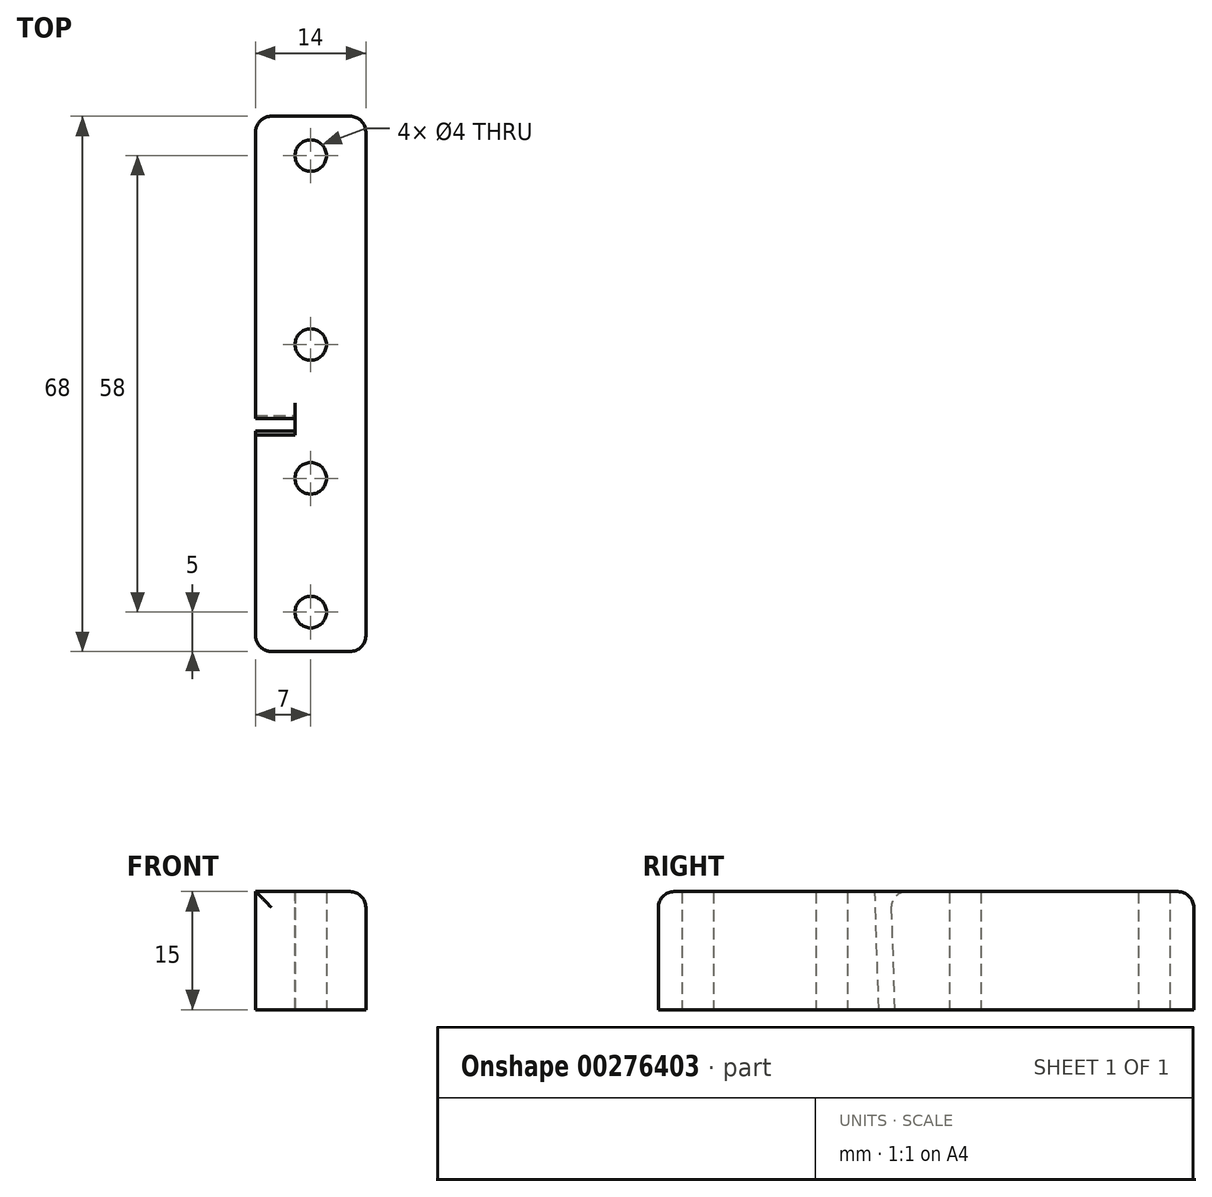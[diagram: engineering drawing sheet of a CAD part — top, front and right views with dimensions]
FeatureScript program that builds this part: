
annotation { "Feature Type Name" : "Feature", "Feature Type Description" : "" }
export const myFeature = defineFeature(function(context is Context, id is Id, definition is map)
    precondition{}
    {
        {
            var Q0;
            Q0=qCreatedBy(makeId("Top.planeOp"),FACE);
            var sketch = newSketch(context, id + "F0", { "sketchPlane" : qUnion([Q0])});
            skLineSegment(sketch, "E0.bottom", {"start": v(0, 0) * mm, "end": v(14, 0) * mm});
            skLineSegment(sketch, "E0.top", {"start": v(0, 68) * mm, "end": v(14, 68) * mm});
            skLineSegment(sketch, "E0.left", {"start": v(0, 0) * mm, "end": v(0, 28) * mm});
            skLineSegment(sketch, "E0.right", {"start": v(14, 0) * mm, "end": v(14, 28) * mm});
            skCircle(sketch, "E1", {"center": v(7, 5) * mm, "radius": 2 * mm});
            skPoint(sketch, "E1.centerSnap0", {"position": v(7, 0) * mm});
            skCircle(sketch, "E2", {"center": v(7, 22) * mm, "radius": 2 * mm});
            skLineSegment(sketch, "E3.bottom", {"start": v(0, 30) * mm, "end": v(14, 30) * mm});
            skLineSegment(sketch, "E3.top", {"start": v(0, 28) * mm, "end": v(14, 28) * mm});
            skLineSegment(sketch, "E4.trimOffspring", {"start": v(0, 30) * mm, "end": v(0, 68) * mm});
            skCircle(sketch, "E5", {"center": v(7, 39) * mm, "radius": 2 * mm});
            skLineSegment(sketch, "E6.trimOffspring", {"start": v(14, 30) * mm, "end": v(14, 68) * mm});
            skCircle(sketch, "E7", {"center": v(7, 63) * mm, "radius": 2 * mm});
            skSolve(sketch);
        }
        {
            var Q0;
            Q0=qSketchRegion(id+"F0",true);
            extrude(context, id + "F1", {"entities" : qUnion([Q0]), "offsetDistance" : 25 * mm, "depth" : 15 * mm});
        }
        {
            var Q0;
            Q0=makeQuery(id+"F1.opExtrude","SWEPT_FACE",FACE,{"disambiguationData":[OSD([sQuery(id+"F0.wireOp",EDGE,"E0.right")])]});
            var sketch = newSketch(context, id + "F2", { "sketchPlane" : qUnion([Q0])});
            skLineSegment(sketch, "E8.bottom", {"start": v(28, 15) * mm, "end": v(30.63, 15) * mm});
            skLineSegment(sketch, "E8.top", {"start": v(28, 0) * mm, "end": v(30.63, 0) * mm});
            skLineSegment(sketch, "E8.left", {"start": v(28, 15) * mm, "end": v(28, 0) * mm});
            skLineSegment(sketch, "E8.right", {"start": v(30.63, 15) * mm, "end": v(30.63, 0) * mm});
            skSolve(sketch);
        }
        {
            var Q0;
            Q0=qSketchRegion(id+"F2",true);
            extrude(context, id + "F3", {"entities" : qUnion([Q0]), "operationType" : NewBodyOperationType.ADD, "oppositeDirection" : true, "depth" : 9 * mm, "offsetDistance" : 25 * mm});
        }
        {
            var Q0;
            Q0=makeQuery(id+"F1.opExtrude","SWEPT_FACE",FACE,{"disambiguationData":[OSD([sQuery(id+"F0.wireOp",EDGE,"E0.left")])]});
            var sketch = newSketch(context, id + "F4", { "sketchPlane" : qUnion([Q0])});
            skLineSegment(sketch, "E9", {"start": v(-28, 0) * mm, "end": v(-27.5, 15) * mm});
            skLineSegment(sketch, "E10", {"start": v(-27.5, 15) * mm, "end": v(-28, 15) * mm});
            skLineSegment(sketch, "E11", {"start": v(-28, 15) * mm, "end": v(-28, 0) * mm});
            skSolve(sketch);
        }
        {
            var Q0;
            Q0 = qSketchRegion(id + "F4", true);
            extrude(context, id + "F5", {"entities" : qUnion([Q0]), "operationType" : NewBodyOperationType.REMOVE, "oppositeDirection" : true, "depth" : 5 * mm, "offsetDistance" : 25 * mm});
        }
        {
            var Q0;
            Q0=makeQuery(id+"F1.opExtrude","SWEPT_FACE",FACE,{"disambiguationData":[OSD([sQuery(id+"F0.wireOp",EDGE,"E4.trimOffspring")])]});
            var sketch = newSketch(context, id + "F6", { "sketchPlane" : qUnion([Q0])});
            skLineSegment(sketch, "E12", {"start": v(-30, 15) * mm, "end": v(-29.5, 15) * mm});
            skLineSegment(sketch, "E13", {"start": v(-29.5, 15) * mm, "end": v(-30, 0) * mm});
            skLineSegment(sketch, "E14", {"start": v(-30, 0) * mm, "end": v(-30, 15) * mm});
            skSolve(sketch);
        }
        {
            var Q0;
            Q0 = qSketchRegion(id + "F6", true);
            extrude(context, id + "F7", {"entities" : qUnion([Q0]), "operationType" : NewBodyOperationType.ADD, "oppositeDirection" : true, "depth" : 5 * mm, "offsetDistance" : 25 * mm});
        }
        {
            var Q0;
            Q0=makeQuery(id+"F7.opExtrude","SWEPT_EDGE",EDGE,{"disambiguationData":[OSD([sQuery(id+"F6.wireOp",EDGE,"E12"),sQuery(id+"F6.wireOp",EDGE,"E13")])]});
            var Q1;
            Q1=makeQuery(id+"F5.boolean.opBoolean","MERGE",EDGE,{"derivedFrom":[makeQuery(id+"F3.opExtrude","CAP_EDGE",EDGE,{"disambiguationData":[OSD([sQuery(id+"F2.wireOp",EDGE,"E8.bottom")])],"isStart":false}),makeQuery(id+"F5.opExtrude","CAP_EDGE",EDGE,{"disambiguationData":[OSD([sQuery(id+"F4.wireOp",EDGE,"E10")])],"isStart":false})]});
            var Q2;
            Q2=makeQuery(id+"F5.boolean.opBoolean","COPY",EDGE,{"derivedFrom":makeQuery(id+"F5.opExtrude","SWEPT_EDGE",EDGE,{"disambiguationData":[OSD([sQuery(id+"F0.wireOp",EDGE,"E0.left"),sQuery(id+"F4.wireOp",EDGE,"E9"),sQuery(id+"F4.wireOp",EDGE,"E10")])]})});
            var Q3;
            Q3=makeQuery(id+"F1.opExtrude","CAP_EDGE",EDGE,{"disambiguationData":[OSD([sQuery(id+"F0.wireOp",EDGE,"E0.bottom")])],"isStart":false});
            var Q4;
            Q4=makeQuery(id+"F3.boolean.opBoolean","MERGE",EDGE,{"derivedFrom":[makeQuery(id+"F1.opExtrude","CAP_EDGE",EDGE,{"disambiguationData":[OSD([sQuery(id+"F0.wireOp",EDGE,"E0.right")])],"isStart":false}),makeQuery(id+"F1.opExtrude","CAP_EDGE",EDGE,{"disambiguationData":[OSD([sQuery(id+"F0.wireOp",EDGE,"E6.trimOffspring")])],"isStart":false}),makeQuery(id+"F3.opExtrude","CAP_EDGE",EDGE,{"disambiguationData":[OSD([sQuery(id+"F2.wireOp",EDGE,"E8.bottom")])],"isStart":true})]});
            var Q5;
            Q5=makeQuery(id+"F1.opExtrude","CAP_EDGE",EDGE,{"disambiguationData":[OSD([sQuery(id+"F0.wireOp",EDGE,"E0.top")])],"isStart":false});
            var Q6;
            Q6=makeQuery(id+"F1.opExtrude","SWEPT_EDGE",EDGE,{"disambiguationData":[OSD([sQuery(id+"F0.wireOp",EDGE,"E0.bottom"),sQuery(id+"F0.wireOp",EDGE,"E0.right")])]});
            var Q7;
            Q7=makeQuery(id+"F1.opExtrude","SWEPT_EDGE",EDGE,{"disambiguationData":[OSD([sQuery(id+"F0.wireOp",EDGE,"E0.top"),sQuery(id+"F0.wireOp",EDGE,"E6.trimOffspring")])]});
            var Q8;
            Q8=makeQuery(id+"F1.opExtrude","SWEPT_EDGE",EDGE,{"disambiguationData":[OSD([sQuery(id+"F0.wireOp",EDGE,"E0.top"),sQuery(id+"F0.wireOp",EDGE,"E4.trimOffspring")])]});
            var Q9;
            Q9=makeQuery(id+"F1.opExtrude","SWEPT_EDGE",EDGE,{"disambiguationData":[OSD([sQuery(id+"F0.wireOp",EDGE,"E0.bottom"),sQuery(id+"F0.wireOp",EDGE,"E0.left")])]});
            fillet(context, id + "F8", {"entities" : qUnion([Q0, Q1, Q2, Q3, Q4, Q5, Q6, Q7, Q8, Q9]), "radius" : 2 * mm, "tangentPropagation" : true, "defaultsChanged" : false, "vertexSettings" : [], "allowEdgeOverflow" : false});
        }
    });
